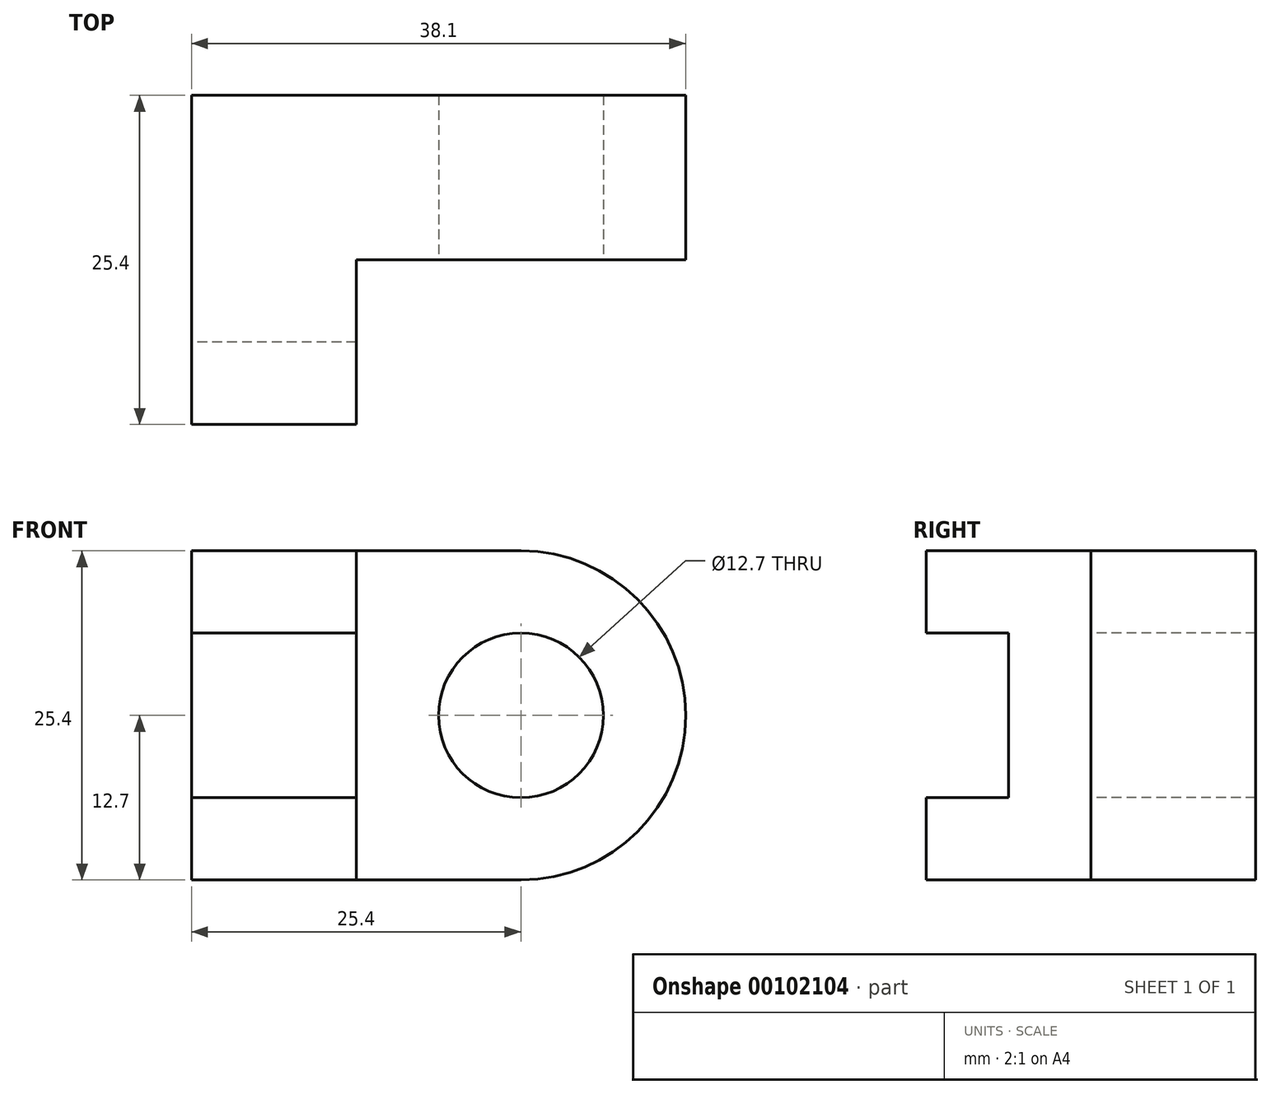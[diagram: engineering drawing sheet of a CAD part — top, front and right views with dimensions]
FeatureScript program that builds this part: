
annotation { "Feature Type Name" : "Feature", "Feature Type Description" : "" }
export const myFeature = defineFeature(function(context is Context, id is Id, definition is map)
    precondition{}
    {
        {
            var Q0;
            Q0=qCreatedBy(makeId("Front.planeOp"),FACE);
            var sketch = newSketch(context, id + "F0", { "sketchPlane" : qUnion([Q0])});
            skLineSegment(sketch, "E0.bottom", {"start": v(0, 0) * mm, "end": v(25.4, 0) * mm});
            skLineSegment(sketch, "E0.top", {"start": v(0, 25.4) * mm, "end": v(25.4, 25.4) * mm});
            skLineSegment(sketch, "E0.left", {"start": v(0, 0) * mm, "end": v(0, 25.4) * mm});
            skLineSegment(sketch, "E0.right", {"start": v(25.4, 0) * mm, "end": v(25.4, 25.4) * mm});
            skArc(sketch, "E1", {"start": v(25.4, 0) * mm, "mid": v(38.1, 12.7) * mm, "end": v(25.4, 25.4) * mm});
            skCircle(sketch, "E2", {"center": v(25.4, 12.7) * mm, "radius": 6.35 * mm});
            skSolve(sketch);
        }
        {
            var Q0;
            Q0 = qSketchRegion(id + "F0", true);
            extrude(context, id + "F1", {"entities" : qUnion([Q0]), "oppositeDirection" : true, "depth" : 12.7 * mm});
        }
        {
            var Q0;
            Q0=qCreatedBy(makeId("Right.planeOp"),FACE);
            var sketch = newSketch(context, id + "F2", { "sketchPlane" : qUnion([Q0])});
            skLineSegment(sketch, "E3", {"start": v(0, 0) * mm, "end": v(0, 25.4) * mm});
            skLineSegment(sketch, "E4", {"start": v(0, 25.4) * mm, "end": v(-12.7, 25.4) * mm});
            skLineSegment(sketch, "E5", {"start": v(-12.7, 25.4) * mm, "end": v(-12.7, 19.05) * mm});
            skLineSegment(sketch, "E6", {"start": v(-12.7, 19.05) * mm, "end": v(-6.35, 19.05) * mm});
            skLineSegment(sketch, "E7", {"start": v(-6.35, 19.05) * mm, "end": v(-6.35, 6.35) * mm});
            skLineSegment(sketch, "E8", {"start": v(-6.35, 6.35) * mm, "end": v(-12.7, 6.35) * mm});
            skLineSegment(sketch, "E9", {"start": v(-12.7, 6.35) * mm, "end": v(-12.7, 0) * mm});
            skLineSegment(sketch, "E10", {"start": v(-12.7, 0) * mm, "end": v(0, 0) * mm});
            skSolve(sketch);
        }
        {
            var Q0;
            Q0 = qSketchRegion(id + "F2", true);
            extrude(context, id + "F3", {"entities" : qUnion([Q0]), "operationType" : NewBodyOperationType.ADD, "depth" : 12.7 * mm});
        }
    });
